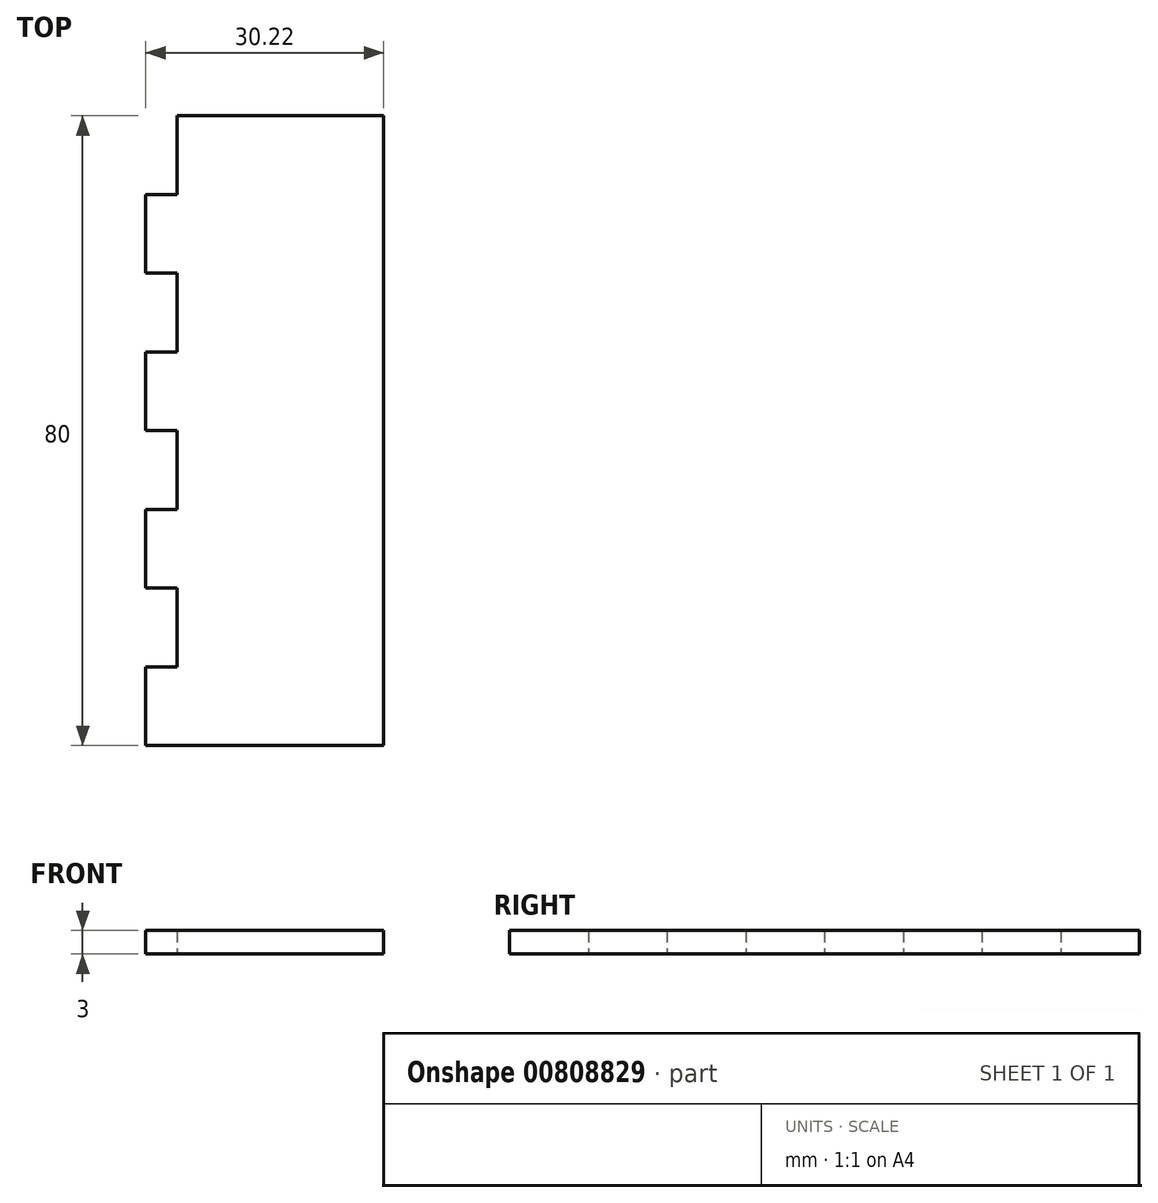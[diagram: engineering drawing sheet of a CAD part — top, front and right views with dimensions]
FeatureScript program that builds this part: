
annotation { "Feature Type Name" : "Feature", "Feature Type Description" : "" }
export const myFeature = defineFeature(function(context is Context, id is Id, definition is map)
    precondition{}
    {
        {
            var Q0;
            Q0=qCreatedBy(makeId("Top.planeOp"),FACE);
            var sketch = newSketch(context, id + "F0", { "sketchPlane" : qUnion([Q0])});
            skLineSegment(sketch, "E0.bottom", {"start": v(-13.61, 40) * mm, "end": v(13.61, 40) * mm});
            skLineSegment(sketch, "E0.top", {"start": v(-13.61, -40) * mm, "end": v(13.61, -40) * mm});
            skLineSegment(sketch, "E0.left", {"start": v(-13.61, 40) * mm, "end": v(-13.61, -40) * mm});
            skLineSegment(sketch, "E0.right", {"start": v(13.61, 40) * mm, "end": v(13.61, -40) * mm});
            skPoint(sketch, "E0.middle", {"position": v(0, 0) * mm});
            skLineSegment(sketch, "E1.bottom", {"start": v(-9.66, -40) * mm, "end": v(-6.66, -40) * mm});
            skLineSegment(sketch, "E1.top", {"start": v(-9.66, -43) * mm, "end": v(-6.66, -43) * mm});
            skLineSegment(sketch, "E1.left", {"start": v(-9.66, -40) * mm, "end": v(-9.66, -43) * mm});
            skLineSegment(sketch, "E1.right", {"start": v(-6.66, -40) * mm, "end": v(-6.66, -43) * mm});
            skLineSegment(sketch, "E2.bottom", {"start": v(2.34, -40) * mm, "end": v(5.34, -40) * mm});
            skLineSegment(sketch, "E2.top", {"start": v(2.34, -43) * mm, "end": v(5.34, -43) * mm});
            skLineSegment(sketch, "E2.left", {"start": v(2.34, -40) * mm, "end": v(2.34, -43) * mm});
            skLineSegment(sketch, "E2.right", {"start": v(5.34, -40) * mm, "end": v(5.34, -43) * mm});
            skLineSegment(sketch, "E3.bottom", {"start": v(8.34, -40) * mm, "end": v(11.34, -40) * mm});
            skLineSegment(sketch, "E3.top", {"start": v(8.34, -43) * mm, "end": v(11.34, -43) * mm});
            skLineSegment(sketch, "E3.left", {"start": v(8.34, -40) * mm, "end": v(8.34, -43) * mm});
            skLineSegment(sketch, "E3.right", {"start": v(11.34, -40) * mm, "end": v(11.34, -43) * mm});
            skLineSegment(sketch, "E4.bottom", {"start": v(-13.61, -40) * mm, "end": v(-16.61, -40) * mm});
            skLineSegment(sketch, "E4.top", {"start": v(-13.61, -30) * mm, "end": v(-16.61, -30) * mm});
            skLineSegment(sketch, "E4.left", {"start": v(-13.61, -40) * mm, "end": v(-13.61, -30) * mm});
            skLineSegment(sketch, "E4.right", {"start": v(-16.61, -40) * mm, "end": v(-16.61, -30) * mm});
            skLineSegment(sketch, "E5.0.1.0", {"start": v(-13.61, -20) * mm, "end": v(-16.61, -20) * mm});
            skLineSegment(sketch, "E5.0.1.1", {"start": v(-16.61, -30) * mm, "end": v(-16.61, -20) * mm});
            skLineSegment(sketch, "E5.0.2.0", {"start": v(-13.61, -10) * mm, "end": v(-16.61, -10) * mm});
            skLineSegment(sketch, "E5.0.2.1", {"start": v(-16.61, -20) * mm, "end": v(-16.61, -10) * mm});
            skLineSegment(sketch, "E5.0.2.2", {"start": v(-13.61, -20) * mm, "end": v(-16.61, -20) * mm});
            skLineSegment(sketch, "E5.0.3.0", {"start": v(-13.61, 0) * mm, "end": v(-16.61, 0) * mm});
            skLineSegment(sketch, "E5.0.3.1", {"start": v(-16.61, -10) * mm, "end": v(-16.61, 0) * mm});
            skLineSegment(sketch, "E5.0.3.2", {"start": v(-13.61, -10) * mm, "end": v(-16.61, -10) * mm});
            skLineSegment(sketch, "E5.0.4.0", {"start": v(-13.61, 10) * mm, "end": v(-16.61, 10) * mm});
            skLineSegment(sketch, "E5.0.4.1", {"start": v(-16.61, 0) * mm, "end": v(-16.61, 10) * mm});
            skLineSegment(sketch, "E5.0.4.2", {"start": v(-13.61, 0) * mm, "end": v(-16.61, 0) * mm});
            skLineSegment(sketch, "E5.0.5.0", {"start": v(-13.61, 20) * mm, "end": v(-16.61, 20) * mm});
            skLineSegment(sketch, "E5.0.5.1", {"start": v(-16.61, 10) * mm, "end": v(-16.61, 20) * mm});
            skLineSegment(sketch, "E5.0.5.2", {"start": v(-13.61, 10) * mm, "end": v(-16.61, 10) * mm});
            skLineSegment(sketch, "E5.0.6.0", {"start": v(-13.61, 30) * mm, "end": v(-16.61, 30) * mm});
            skLineSegment(sketch, "E5.0.6.1", {"start": v(-16.61, 20) * mm, "end": v(-16.61, 30) * mm});
            skLineSegment(sketch, "E5.0.6.2", {"start": v(-13.61, 20) * mm, "end": v(-16.61, 20) * mm});
            skLineSegment(sketch, "E5.0.7.0", {"start": v(-13.61, 40) * mm, "end": v(-16.61, 40) * mm});
            skLineSegment(sketch, "E5.0.7.1", {"start": v(-16.61, 30) * mm, "end": v(-16.61, 40) * mm});
            skLineSegment(sketch, "E5.0.7.2", {"start": v(-13.61, 30) * mm, "end": v(-16.61, 30) * mm});
            skLineSegment(sketch, "E5.direction1", {"start": v(-16.61, -30) * mm, "end": v(8.39, -30) * mm, "construction": true});
            skLineSegment(sketch, "E5.direction2", {"start": v(-16.61, -30) * mm, "end": v(-16.61, -20) * mm, "construction": true});
            skSolve(sketch);
        }
        {
            var Q0;
            Q0=makeQuery(id+"F0.imprint","IMPRINT",FACE,{"disambiguationData":[TD([[makeQuery(id+"F0.imprint","IMPRINT",EDGE,{"derivedFrom":sQuery(id+"F0.wireOp",EDGE,"E1.bottom")}),-1.0]])]});
            var Q1;
            Q1=makeQuery(id+"F0.imprint","IMPRINT",FACE,{"disambiguationData":[TD([[makeQuery(id+"F0.imprint","IMPRINT",EDGE,{"derivedFrom":sQuery(id+"F0.wireOp",EDGE,"E2.bottom")}),-1.0]])]});
            var Q2;
            Q2=makeQuery(id+"F0.imprint","IMPRINT",FACE,{"disambiguationData":[TD([[makeQuery(id+"F0.imprint","IMPRINT",EDGE,{"derivedFrom":sQuery(id+"F0.wireOp",EDGE,"E3.bottom")}),-1.0]])]});
            var Q3;
            Q3=makeQuery(id+"F0.imprint","IMPRINT",FACE,{"disambiguationData":[TD([[makeQuery(id+"F0.imprint","IMPRINT",EDGE,{"derivedFrom":sQuery(id+"F0.wireOp",EDGE,"E4.bottom")}),-1.0]])]});
            var Q4;
            Q4=makeQuery(id+"F0.imprint","IMPRINT",FACE,{"disambiguationData":[TD([[makeQuery(id+"F0.imprint","IMPRINT",EDGE,{"derivedFrom":sQuery(id+"F0.wireOp",EDGE,"E5.0.6.1")}),-1.0]])]});
            var Q5;
            Q5=makeQuery(id+"F0.imprint","IMPRINT",FACE,{"disambiguationData":[TD([[makeQuery(id+"F0.imprint","IMPRINT",EDGE,{"derivedFrom":sQuery(id+"F0.wireOp",EDGE,"E5.0.4.1")}),-1.0]])]});
            var Q6;
            Q6=makeQuery(id+"F0.imprint","IMPRINT",FACE,{"disambiguationData":[TD([[makeQuery(id+"F0.imprint","IMPRINT",EDGE,{"derivedFrom":sQuery(id+"F0.wireOp",EDGE,"E5.0.2.1")}),-1.0]])]});
            var Q7;
            {var subQ6=sQuery(id+"F0.wireOp",EDGE,"E0.bottom");Q7=makeQuery(id+"F0.imprint","IMPRINT",FACE,{"disambiguationData":[TD([[makeQuery(id+"F0.imprint","IMPRINT",EDGE,{"derivedFrom":subQ6}),-1.0]])]});}
            extrude(context, id + "F1", {"entities" : qUnion([Q0, Q1, Q2, Q3, Q4, Q5, Q6, Q7]), "depth" : 3 * mm, "offsetDistance" : 25 * mm});
        }
        {
            var Q0;
            Q0=makeQuery(id+"F1.opExtrude","CAP_FACE",FACE,{"disambiguationData":[OSD([sQuery(id+"F0.wireOp",EDGE,"E0.bottom"),sQuery(id+"F0.wireOp",EDGE,"E0.top"),sQuery(id+"F0.wireOp",EDGE,"E0.left"),sQuery(id+"F0.wireOp",EDGE,"E0.right"),sQuery(id+"F0.wireOp",EDGE,"E1.top"),sQuery(id+"F0.wireOp",EDGE,"E1.left"),sQuery(id+"F0.wireOp",EDGE,"E1.right"),sQuery(id+"F0.wireOp",EDGE,"E2.top"),sQuery(id+"F0.wireOp",EDGE,"E2.left"),sQuery(id+"F0.wireOp",EDGE,"E2.right"),sQuery(id+"F0.wireOp",EDGE,"E3.top"),sQuery(id+"F0.wireOp",EDGE,"E3.left"),sQuery(id+"F0.wireOp",EDGE,"E3.right"),sQuery(id+"F0.wireOp",EDGE,"E4.bottom"),sQuery(id+"F0.wireOp",EDGE,"E4.right"),sQuery(id+"F0.wireOp",EDGE,"E4.top"),sQuery(id+"F0.wireOp",EDGE,"E5.0.2.1"),sQuery(id+"F0.wireOp",EDGE,"E5.0.2.2"),sQuery(id+"F0.wireOp",EDGE,"E5.0.3.2"),sQuery(id+"F0.wireOp",EDGE,"E5.0.4.1"),sQuery(id+"F0.wireOp",EDGE,"E5.0.4.2"),sQuery(id+"F0.wireOp",EDGE,"E5.0.5.2"),sQuery(id+"F0.wireOp",EDGE,"E5.0.6.1"),sQuery(id+"F0.wireOp",EDGE,"E5.0.6.2"),sQuery(id+"F0.wireOp",EDGE,"E5.0.7.2")])],"isStart":true});
            var sketch = newSketch(context, id + "F2", { "sketchPlane" : qUnion([Q0])});
            skLineSegment(sketch, "E6.bottom", {"start": v(-13.61, -40) * mm, "end": v(-12.61, -40) * mm});
            skLineSegment(sketch, "E6.top", {"start": v(-13.61, -30) * mm, "end": v(-12.61, -30) * mm});
            skLineSegment(sketch, "E6.left", {"start": v(-13.61, -40) * mm, "end": v(-13.61, -30) * mm});
            skLineSegment(sketch, "E6.right", {"start": v(-12.61, -40) * mm, "end": v(-12.61, -30) * mm});
            skLineSegment(sketch, "E7.0.1.0", {"start": v(-12.61, -20) * mm, "end": v(-12.61, -10) * mm});
            skLineSegment(sketch, "E7.0.1.1", {"start": v(-13.61, -10) * mm, "end": v(-12.61, -10) * mm});
            skLineSegment(sketch, "E7.0.1.2", {"start": v(-13.61, -20) * mm, "end": v(-13.61, -10) * mm});
            skLineSegment(sketch, "E7.0.1.3", {"start": v(-13.61, -20) * mm, "end": v(-12.61, -20) * mm});
            skLineSegment(sketch, "E7.0.2.0", {"start": v(-12.61, 0) * mm, "end": v(-12.61, 10) * mm});
            skLineSegment(sketch, "E7.0.2.1", {"start": v(-13.61, 10) * mm, "end": v(-12.61, 10) * mm});
            skLineSegment(sketch, "E7.0.2.2", {"start": v(-13.61, 0) * mm, "end": v(-13.61, 10) * mm});
            skLineSegment(sketch, "E7.0.2.3", {"start": v(-13.61, 0) * mm, "end": v(-12.61, 0) * mm});
            skLineSegment(sketch, "E7.0.3.0", {"start": v(-12.61, 20) * mm, "end": v(-12.61, 30) * mm});
            skLineSegment(sketch, "E7.0.3.1", {"start": v(-13.61, 30) * mm, "end": v(-12.61, 30) * mm});
            skLineSegment(sketch, "E7.0.3.2", {"start": v(-13.61, 20) * mm, "end": v(-13.61, 30) * mm});
            skLineSegment(sketch, "E7.0.3.3", {"start": v(-13.61, 20) * mm, "end": v(-12.61, 20) * mm});
            skLineSegment(sketch, "E7.direction1", {"start": v(-12.61, -40) * mm, "end": v(12.39, -40) * mm, "construction": true});
            skLineSegment(sketch, "E7.direction2", {"start": v(-12.61, -40) * mm, "end": v(-12.61, -20) * mm, "construction": true});
            skSolve(sketch);
        }
        {
            var Q0;
            Q0=qSketchRegion(id+"F2",true);
            extrude(context, id + "F3", {"entities" : qUnion([Q0]), "operationType" : NewBodyOperationType.REMOVE, "oppositeDirection" : true, "depth" : 25 * mm, "offsetDistance" : 25 * mm});
        }
    });
